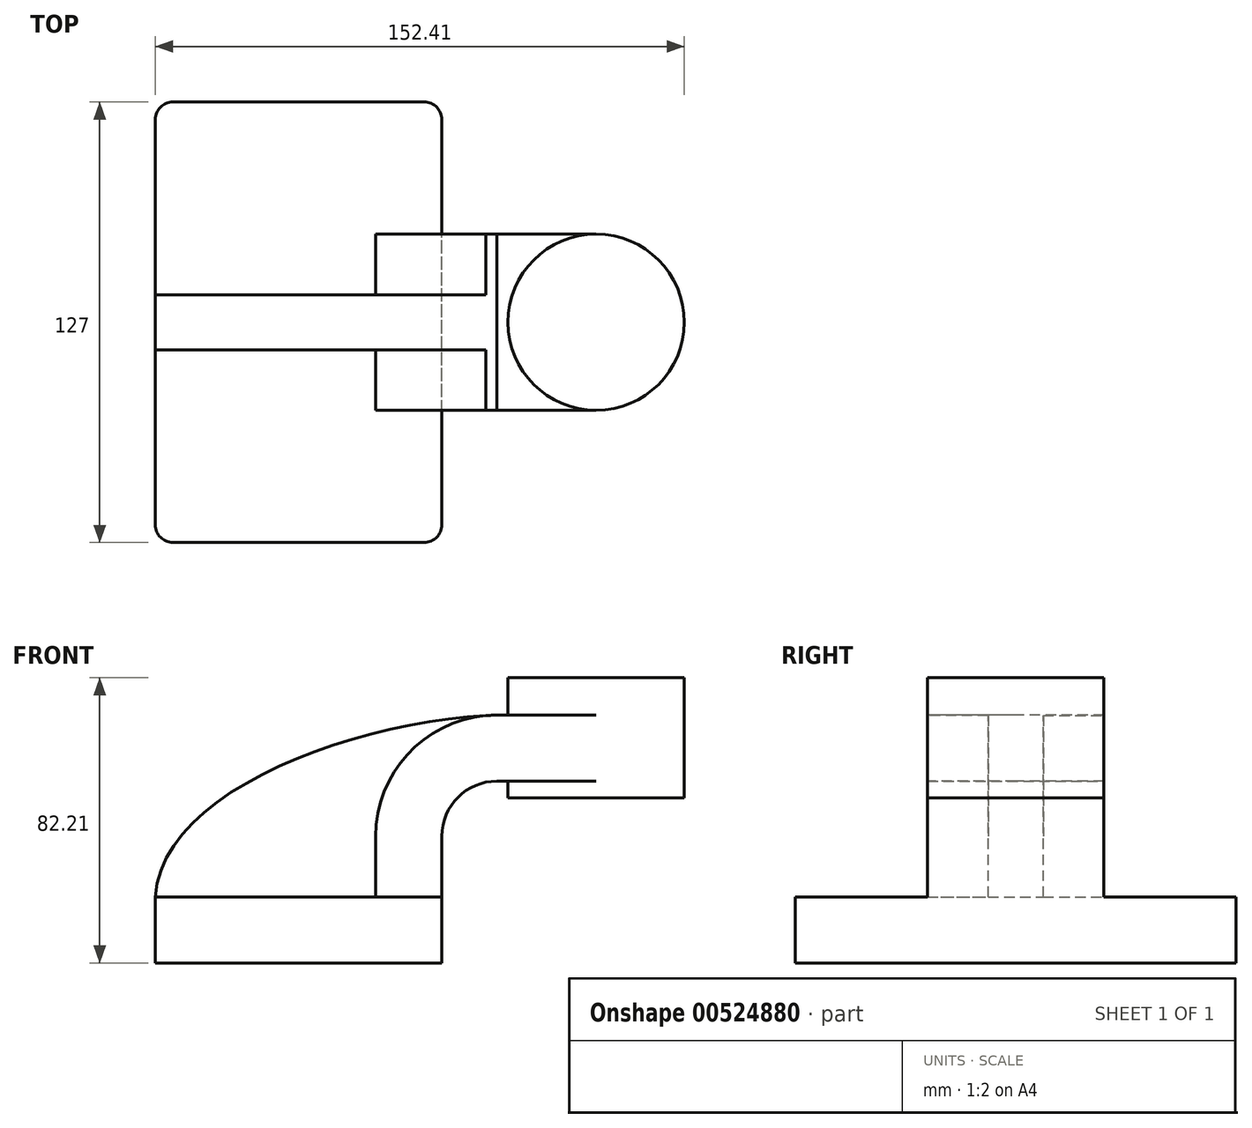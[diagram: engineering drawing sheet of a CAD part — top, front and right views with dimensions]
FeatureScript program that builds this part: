
annotation { "Feature Type Name" : "Feature", "Feature Type Description" : "" }
export const myFeature = defineFeature(function(context is Context, id is Id, definition is map)
    precondition{}
    {
        {
            var Q0;
            Q0=qCreatedBy(makeId("Front.planeOp"),FACE);
            var sketch = newSketch(context, id + "F0", { "sketchPlane" : qUnion([Q0])});
            skLineSegment(sketch, "E0.rect.bottom", {"start": v(-41.28, 9.52) * mm, "end": v(41.28, 9.52) * mm});
            skLineSegment(sketch, "E0.rect.top", {"start": v(-41.28, -9.52) * mm, "end": v(41.28, -9.52) * mm});
            skLineSegment(sketch, "E0.rect.left", {"start": v(-41.28, 9.52) * mm, "end": v(-41.28, -9.52) * mm});
            skLineSegment(sketch, "E0.rect.right", {"start": v(41.28, 9.52) * mm, "end": v(41.28, -9.52) * mm});
            skPoint(sketch, "E0.rect.middle", {"position": v(0, 0) * mm});
            skLineSegment(sketch, "E1", {"start": v(41.28, 9.52) * mm, "end": v(41.28, 27) * mm});
            skArc(sketch, "E2", {"start": v(41.28, 27) * mm, "mid": v(45.92, 38.23) * mm, "end": v(57.15, 42.88) * mm});
            skLineSegment(sketch, "E3", {"start": v(57.15, 42.88) * mm, "end": v(85.72, 42.88) * mm});
            skLineSegment(sketch, "E4.rect.bottom", {"start": v(60.32, 38.1) * mm, "end": v(111.12, 38.1) * mm});
            skLineSegment(sketch, "E4.rect.top", {"start": v(60.32, 66.68) * mm, "end": v(111.12, 66.68) * mm});
            skLineSegment(sketch, "E4.rect.left", {"start": v(60.32, 38.1) * mm, "end": v(60.32, 66.68) * mm});
            skLineSegment(sketch, "E4.rect.right", {"start": v(111.13, 38.1) * mm, "end": v(111.12, 66.68) * mm});
            skPoint(sketch, "E4.rect.middle", {"position": v(85.72, 52.39) * mm});
            skLineSegment(sketch, "E5.0", {"start": v(57.15, 61.93) * mm, "end": v(85.72, 61.93) * mm});
            skArc(sketch, "E5.1", {"start": v(22.23, 27) * mm, "mid": v(32.45, 51.7) * mm, "end": v(57.15, 61.93) * mm});
            skLineSegment(sketch, "E5.2", {"start": v(22.23, 9.52) * mm, "end": v(22.23, 27) * mm});
            skLineSegment(sketch, "E6", {"start": v(85.72, 38.1) * mm, "end": v(85.72, 66.68) * mm});
            skFitSpline(sketch, "E7", {"points": [v(-41.28, 9.53) * mm, v(57.15, 61.93) * mm], "startDerivative": vector(5.2, 92.34) * mm, "endDerivative": vector(120.92, 4.22) * mm});
            skSolve(sketch);
        }
        {
            var Q0;
            Q0=makeQuery(id+"F0.imprint","IMPRINT",FACE,{"disambiguationData":[TD([[makeQuery(id+"F0.imprint","IMPRINT",EDGE,{"derivedFrom":sQuery(id+"F0.wireOp",EDGE,"E0.rect.top")}),1.0]])]});
            extrude(context, id + "F1", {"entities" : qUnion([Q0]), "endBound" : BoundingType.SYMMETRIC, "depth" : 127 * mm});
        }
        {
            var Q0;
            {var subQ9=sQuery(id+"F0.wireOp",EDGE,"E1");Q0=makeQuery(id+"F0.imprint","IMPRINT",FACE,{"disambiguationData":[TD([[makeQuery(id+"F0.imprint","IMPRINT",EDGE,{"derivedFrom":subQ9}),1.0]])]});}
            var Q1;
            {var subQ0=sQuery(id+"F0.wireOp",EDGE,"E6");var subQ1=sQuery(id+"F0.wireOp",EDGE,"E3");var subQ2=makeQuery(id+"F0.imprint","INTERSECT",VERTEX,{"derivedFrom":[subQ1,subQ0]});Q1=makeQuery(id+"F0.imprint","IMPRINT",FACE,{"disambiguationData":[TD([[makeQuery(id+"F0.imprint","IMPRINT",EDGE,{"disambiguationData":[TD([[subQ2,1.0]])],"derivedFrom":subQ1}),1.0]])]});}
            extrude(context, id + "F2", {"entities" : qUnion([Q0, Q1]), "operationType" : NewBodyOperationType.ADD, "endBound" : BoundingType.SYMMETRIC, "depth" : 50.8 * mm});
        }
        {
            var Q0;
            {var subQ3=sQuery(id+"F0.wireOp",EDGE,"E5.2");Q0=makeQuery(id+"F0.imprint","IMPRINT",FACE,{"disambiguationData":[TD([[makeQuery(id+"F0.imprint","IMPRINT",EDGE,{"derivedFrom":subQ3}),1.0]])]});}
            extrude(context, id + "F3", {"entities" : qUnion([Q0]), "operationType" : NewBodyOperationType.ADD, "endBound" : BoundingType.SYMMETRIC, "depth" : 15.88 * mm});
        }
        {
            var Q0;
            {var subQ5=sQuery(id+"F0.wireOp",EDGE,"E4.rect.right");Q0=makeQuery(id+"F0.imprint","IMPRINT",FACE,{"disambiguationData":[TD([[makeQuery(id+"F0.imprint","IMPRINT",EDGE,{"derivedFrom":subQ5}),1.0]])]});}
            var Q1;
            Q1=sQuery(id+"F0.wireOp",EDGE,"E6");
            revolve(context, id + "F4", {"operationType" : NewBodyOperationType.ADD, "entities" : qUnion([Q0]), "axis" : qUnion([Q1]), "revolveType" : RevolveType.FULL});
        }
        {
            var Q0;
            Q0=makeQuery(id+"F1.opExtrude","CAP_EDGE",EDGE,{"disambiguationData":[OSD([sQuery(id+"F0.wireOp",EDGE,"E0.rect.right")])],"isStart":false});
            var Q1;
            Q1=makeQuery(id+"F1.opExtrude","CAP_EDGE",EDGE,{"disambiguationData":[OSD([sQuery(id+"F0.wireOp",EDGE,"E0.rect.left")])],"isStart":false});
            var Q2;
            Q2=makeQuery(id+"F1.opExtrude","CAP_EDGE",EDGE,{"disambiguationData":[OSD([sQuery(id+"F0.wireOp",EDGE,"E0.rect.right")])],"isStart":true});
            var Q3;
            Q3=makeQuery(id+"F1.opExtrude","CAP_EDGE",EDGE,{"disambiguationData":[OSD([sQuery(id+"F0.wireOp",EDGE,"E0.rect.left")])],"isStart":true});
            fillet(context, id + "F5", {"entities" : qUnion([Q0, Q1, Q2, Q3]), "radius" : 5.08 * mm, "tangentPropagation" : true, "allowEdgeOverflow" : false});
        }
        {
            var Q0;
            Q0=makeQuery(id+"F4.opRevolve","SWEPT_FACE",FACE,{"disambiguationData":[OSD([sQuery(id+"F0.wireOp",EDGE,"E4.rect.top")])]});
            extrude(context, id + "F6", {"entities" : qUnion([Q0]), "operationType" : NewBodyOperationType.ADD, "depth" : 6 * mm, "offsetDistance" : 25 * mm});
        }
    });
